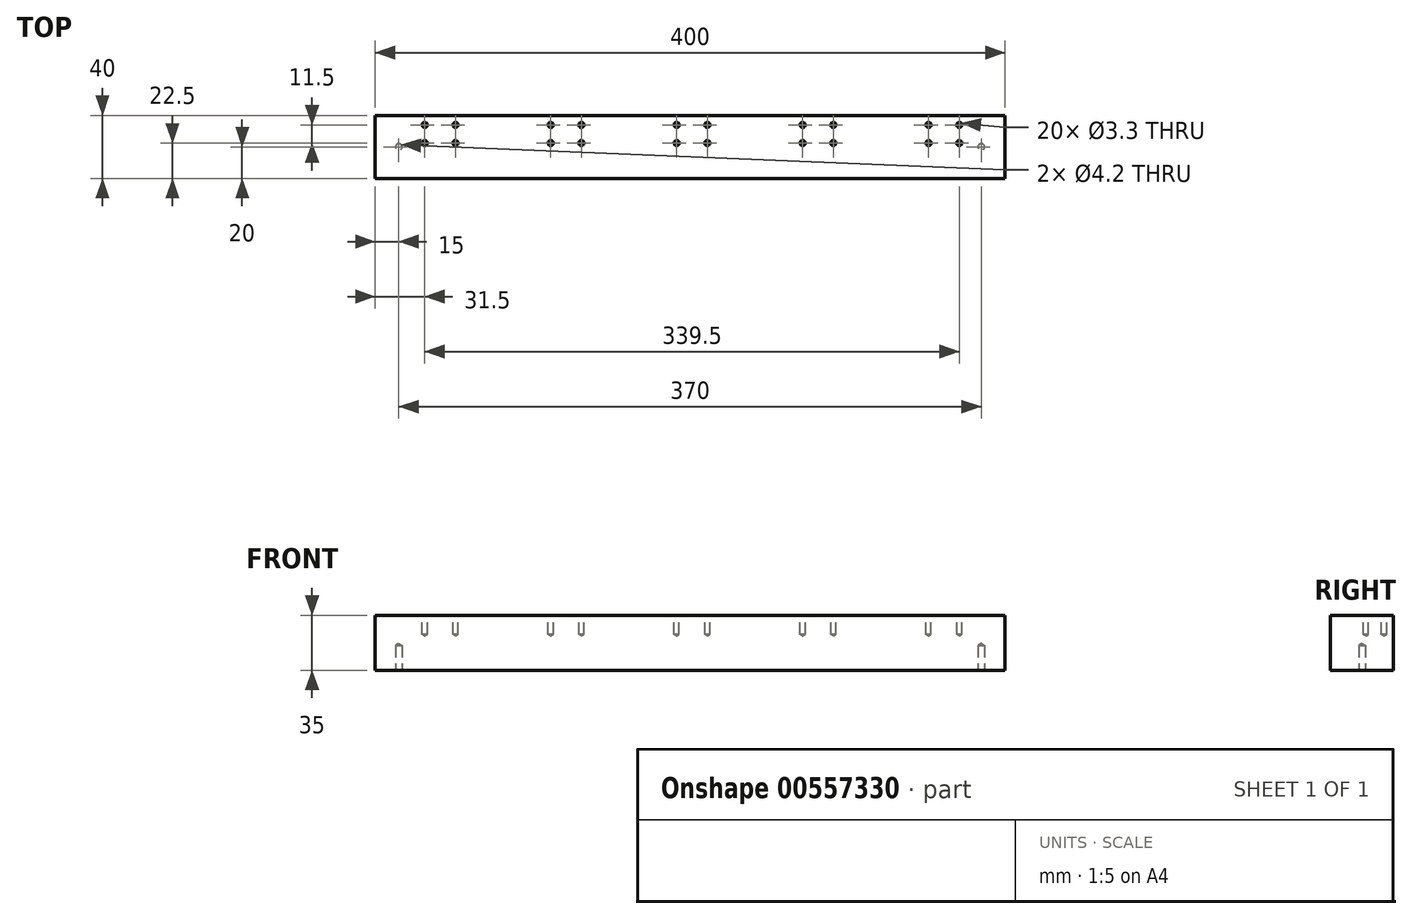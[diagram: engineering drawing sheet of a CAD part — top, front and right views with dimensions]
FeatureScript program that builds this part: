
annotation { "Feature Type Name" : "Feature", "Feature Type Description" : "" }
export const myFeature = defineFeature(function(context is Context, id is Id, definition is map)
    precondition{}
    {
        {
            var Q0;
            Q0=qCreatedBy(makeId("Top.planeOp"),FACE);
            var sketch = newSketch(context, id + "F0", { "sketchPlane" : qUnion([Q0])});
            skLineSegment(sketch, "E0.bottom", {"start": v(0, 0) * mm, "end": v(400, 0) * mm});
            skLineSegment(sketch, "E0.top", {"start": v(0, -40) * mm, "end": v(400, -40) * mm});
            skLineSegment(sketch, "E0.left", {"start": v(0, 0) * mm, "end": v(0, -40) * mm});
            skLineSegment(sketch, "E0.right", {"start": v(400, 0) * mm, "end": v(400, -40) * mm});
            skSolve(sketch);
        }
        {
            var Q0;
            Q0 = qSketchRegion(id + "F0", true);
            extrude(context, id + "F1", {"entities" : qUnion([Q0]), "depth" : 35 * mm, "offsetDistance" : 25 * mm});
        }
        {
            var Q0;
            Q0=makeQuery(id+"F1.opExtrude","CAP_FACE",FACE,{"disambiguationData":[OSD([sQuery(id+"F0.wireOp",EDGE,"E0.bottom"),sQuery(id+"F0.wireOp",EDGE,"E0.top"),sQuery(id+"F0.wireOp",EDGE,"E0.left"),sQuery(id+"F0.wireOp",EDGE,"E0.right")])],"isStart":false});
            var sketch = newSketch(context, id + "F2", { "sketchPlane" : qUnion([Q0])});
            skCircle(sketch, "E1", {"center": v(31.5, -6) * mm, "radius": 1.75 * mm});
            skCircle(sketch, "E2", {"center": v(51, -6) * mm, "radius": 1.75 * mm});
            skCircle(sketch, "E3", {"center": v(31.5, -17.5) * mm, "radius": 1.75 * mm});
            skCircle(sketch, "E4", {"center": v(51, -17.5) * mm, "radius": 1.75 * mm});
            skCircle(sketch, "E5.1.0.0", {"center": v(131, -6) * mm, "radius": 1.75 * mm});
            skCircle(sketch, "E5.1.0.1", {"center": v(111.5, -6) * mm, "radius": 1.75 * mm});
            skCircle(sketch, "E5.1.0.2", {"center": v(111.5, -17.5) * mm, "radius": 1.75 * mm});
            skCircle(sketch, "E5.1.0.3", {"center": v(131, -17.5) * mm, "radius": 1.75 * mm});
            skCircle(sketch, "E5.2.0.0", {"center": v(211, -6) * mm, "radius": 1.75 * mm});
            skCircle(sketch, "E5.2.0.1", {"center": v(191.5, -6) * mm, "radius": 1.75 * mm});
            skCircle(sketch, "E5.2.0.2", {"center": v(191.5, -17.5) * mm, "radius": 1.75 * mm});
            skCircle(sketch, "E5.2.0.3", {"center": v(211, -17.5) * mm, "radius": 1.75 * mm});
            skCircle(sketch, "E5.3.0.0", {"center": v(291, -6) * mm, "radius": 1.75 * mm});
            skCircle(sketch, "E5.3.0.1", {"center": v(271.5, -6) * mm, "radius": 1.75 * mm});
            skCircle(sketch, "E5.3.0.2", {"center": v(271.5, -17.5) * mm, "radius": 1.75 * mm});
            skCircle(sketch, "E5.3.0.3", {"center": v(291, -17.5) * mm, "radius": 1.75 * mm});
            skCircle(sketch, "E5.4.0.0", {"center": v(371, -6) * mm, "radius": 1.75 * mm});
            skCircle(sketch, "E5.4.0.1", {"center": v(351.5, -6) * mm, "radius": 1.75 * mm});
            skCircle(sketch, "E5.4.0.2", {"center": v(351.5, -17.5) * mm, "radius": 1.75 * mm});
            skCircle(sketch, "E5.4.0.3", {"center": v(371, -17.5) * mm, "radius": 1.75 * mm});
            skLineSegment(sketch, "E5.direction1", {"start": v(51, -6) * mm, "end": v(131, -6) * mm, "construction": true});
            skSolve(sketch);
        }
        {
            var Q0;
            Q0=sQuery(id+"F2.wireOp",VERTEX,"E1.center");
            var Q1;
            Q1=sQuery(id+"F2.wireOp",VERTEX,"E2.center");
            var Q2;
            Q2=sQuery(id+"F2.wireOp",VERTEX,"E4.center");
            var Q3;
            Q3=sQuery(id+"F2.wireOp",VERTEX,"E3.center");
            var Q4;
            Q4=sQuery(id+"F2.wireOp",VERTEX,"E5.1.0.1.center");
            var Q5;
            Q5=sQuery(id+"F2.wireOp",VERTEX,"E5.1.0.0.center");
            var Q6;
            Q6=sQuery(id+"F2.wireOp",VERTEX,"E5.1.0.2.center");
            var Q7;
            Q7=sQuery(id+"F2.wireOp",VERTEX,"E5.1.0.3.center");
            var Q8;
            Q8=sQuery(id+"F2.wireOp",VERTEX,"E5.2.0.1.center");
            var Q9;
            Q9=sQuery(id+"F2.wireOp",VERTEX,"E5.2.0.0.center");
            var Q10;
            Q10=sQuery(id+"F2.wireOp",VERTEX,"E5.2.0.2.center");
            var Q11;
            Q11=sQuery(id+"F2.wireOp",VERTEX,"E5.2.0.3.center");
            var Q12;
            Q12=sQuery(id+"F2.wireOp",VERTEX,"E5.3.0.1.center");
            var Q13;
            Q13=sQuery(id+"F2.wireOp",VERTEX,"E5.3.0.2.center");
            var Q14;
            Q14=sQuery(id+"F2.wireOp",VERTEX,"E5.3.0.0.center");
            var Q15;
            Q15=sQuery(id+"F2.wireOp",VERTEX,"E5.3.0.3.center");
            var Q16;
            Q16=sQuery(id+"F2.wireOp",VERTEX,"E5.4.0.1.center");
            var Q17;
            Q17=sQuery(id+"F2.wireOp",VERTEX,"E5.4.0.0.center");
            var Q18;
            Q18=sQuery(id+"F2.wireOp",VERTEX,"E5.4.0.3.center");
            var Q19;
            Q19=sQuery(id+"F2.wireOp",VERTEX,"E5.4.0.2.center");
            var Q20;
            Q20=makeQuery(id+"F1.opExtrude","SWEPT_BODY",BODY,{"disambiguationData":[OSD([sQuery(id+"F0.wireOp",EDGE,"E0.bottom"),sQuery(id+"F0.wireOp",EDGE,"E0.top"),sQuery(id+"F0.wireOp",EDGE,"E0.left"),sQuery(id+"F0.wireOp",EDGE,"E0.right")])]});
            hole(context, id + "F3", {"style" : HoleStyle.SIMPLE, "endStyle" : HoleEndStyle.BLIND, "standardTappedOrClearance" : lookupTablePath({ "standard" : "ISO", "engagement" : "75%", "pitch" : "0.7 mm", "size" : "M4", "type" : "Tapped" }), "standardBlindInLast" : lookupTablePath({ "standard" : "ISO", "engagement" : "75%", "pitch" : "0.7 mm", "size" : "M4", "type" : "Tapped" }), "holeDiameter" : 3.3 * mm, "showTappedDepth" : true, "holeDepth" : 12 * mm, "isTappedThrough" : true, "tappedDepth" : 9.9 * mm, "tapClearance" : 3, "locations" : qUnion([Q0, Q1, Q2, Q3, Q4, Q5, Q6, Q7, Q8, Q9, Q10, Q11, Q12, Q13, Q14, Q15, Q16, Q17, Q18, Q19]), "scope" : qUnion([Q20]), "majorDiameter" : 4 * mm});
        }
        {
            var Q0;
            Q0=makeQuery(id+"F1.opExtrude","CAP_FACE",FACE,{"disambiguationData":[OSD([sQuery(id+"F0.wireOp",EDGE,"E0.bottom"),sQuery(id+"F0.wireOp",EDGE,"E0.top"),sQuery(id+"F0.wireOp",EDGE,"E0.left"),sQuery(id+"F0.wireOp",EDGE,"E0.right")])],"isStart":true});
            var sketch = newSketch(context, id + "F4", { "sketchPlane" : qUnion([Q0])});
            skCircle(sketch, "E6", {"center": v(15, 20) * mm, "radius": 2.5 * mm});
            skCircle(sketch, "E7", {"center": v(385, 20) * mm, "radius": 2.5 * mm});
            skSolve(sketch);
        }
        {
            var Q0;
            Q0=sQuery(id+"F4.wireOp",VERTEX,"E6.center");
            var Q1;
            Q1=sQuery(id+"F4.wireOp",VERTEX,"E7.center");
            var Q2;
            Q2=makeQuery(id+"F1.opExtrude","SWEPT_BODY",BODY,{"disambiguationData":[OSD([sQuery(id+"F0.wireOp",EDGE,"E0.bottom"),sQuery(id+"F0.wireOp",EDGE,"E0.top"),sQuery(id+"F0.wireOp",EDGE,"E0.left"),sQuery(id+"F0.wireOp",EDGE,"E0.right")])]});
            hole(context, id + "F5", {"style" : HoleStyle.SIMPLE, "endStyle" : HoleEndStyle.BLIND, "standardTappedOrClearance" : lookupTablePath({ "standard" : "ISO", "engagement" : "75%", "pitch" : "0.8 mm", "size" : "M5", "type" : "Tapped" }), "standardBlindInLast" : lookupTablePath({ "standard" : "ISO", "engagement" : "75%", "pitch" : "0.8 mm", "size" : "M5", "type" : "Tapped" }), "holeDiameter" : 4.2 * mm, "majorDiameter" : 5 * mm, "showTappedDepth" : true, "holeDepth" : 15.9 * mm, "isTappedThrough" : true, "tappedDepth" : 13.5 * mm, "tapClearance" : 3, "locations" : qUnion([Q0, Q1]), "scope" : qUnion([Q2])});
        }
    });
